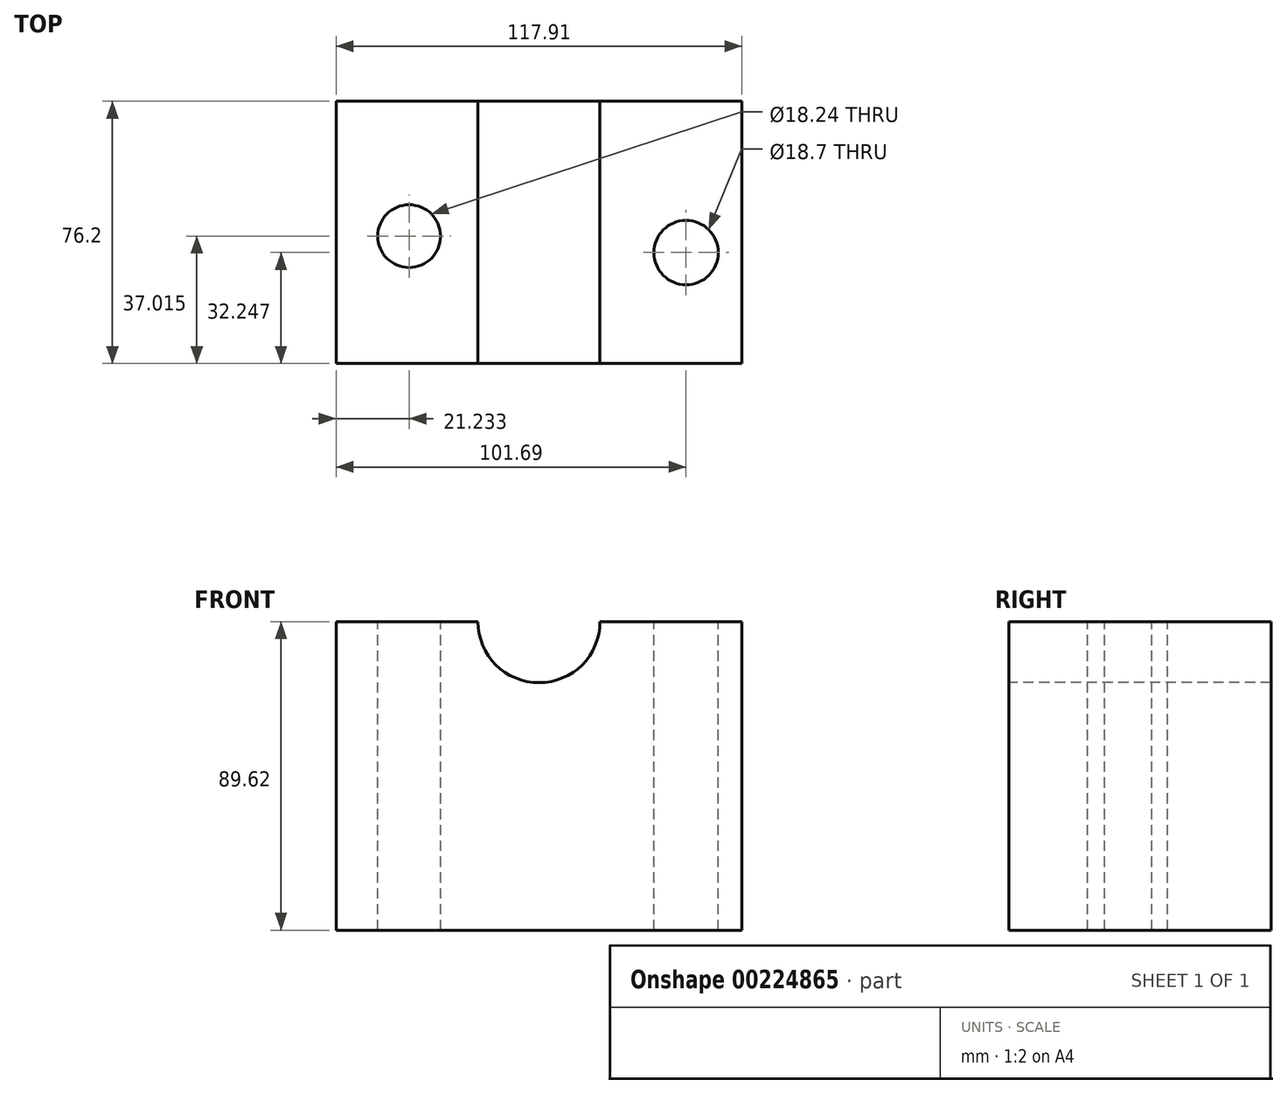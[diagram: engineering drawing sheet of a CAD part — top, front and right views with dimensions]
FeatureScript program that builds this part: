
annotation { "Feature Type Name" : "Feature", "Feature Type Description" : "" }
export const myFeature = defineFeature(function(context is Context, id is Id, definition is map)
    precondition{}
    {
        {
            var Q0;
            Q0=qCreatedBy(makeId("Front.planeOp"),FACE);
            var sketch = newSketch(context, id + "F0", { "sketchPlane" : qUnion([Q0])});
            skLineSegment(sketch, "E0.bottom", {"start": v(-58.78, 45.66) * mm, "end": v(59.13, 45.66) * mm});
            skLineSegment(sketch, "E0.top", {"start": v(-58.78, -43.96) * mm, "end": v(59.13, -43.96) * mm});
            skLineSegment(sketch, "E0.left", {"start": v(-58.78, 45.66) * mm, "end": v(-58.78, -43.96) * mm});
            skLineSegment(sketch, "E0.right", {"start": v(59.13, 45.66) * mm, "end": v(59.13, -43.96) * mm});
            skSolve(sketch);
        }
        {
            var Q0;
            Q0=makeQuery(id+"F0.imprint","IMPRINT",FACE,{"disambiguationData":[TD([[makeQuery(id+"F0.imprint","IMPRINT",EDGE,{"derivedFrom":sQuery(id+"F0.wireOp",EDGE,"E0.bottom")}),-1.0]])]});
            extrude(context, id + "F1", {"entities" : qUnion([Q0]), "depth" : 76.2 * mm});
        }
        {
            var Q0;
            Q0=makeQuery(id+"F1.opExtrude","SWEPT_FACE",FACE,{"disambiguationData":[OSD([sQuery(id+"F0.wireOp",EDGE,"E0.bottom")])]});
            var sketch = newSketch(context, id + "F2", { "sketchPlane" : qUnion([Q0])});
            skCircle(sketch, "E1", {"center": v(-37.55, -39.19) * mm, "radius": 9.12 * mm});
            skSolve(sketch);
        }
        {
            var Q0;
            Q0=makeQuery(id+"F2.imprint","IMPRINT",FACE,{"disambiguationData":[TD([[makeQuery(id+"F2.imprint","IMPRINT",EDGE,{"derivedFrom":sQuery(id+"F2.wireOp",EDGE,"E1")}),-1.0]])]});
            var sketch = newSketch(context, id + "F3", { "sketchPlane" : qUnion([Q0])});
            skCircle(sketch, "E2", {"center": v(42.91, -43.95) * mm, "radius": 9.35 * mm});
            skSolve(sketch);
        }
        {
            var Q0;
            Q0=makeQuery(id+"F2.imprint","IMPRINT",FACE,{"disambiguationData":[TD([[makeQuery(id+"F2.imprint","IMPRINT",EDGE,{"derivedFrom":sQuery(id+"F2.wireOp",EDGE,"E1")}),1.0]])]});
            extrude(context, id + "F4", {"entities" : qUnion([Q0]), "operationType" : NewBodyOperationType.REMOVE, "endBound" : BoundingType.THROUGH_ALL, "oppositeDirection" : true, "depth" : 25.4 * mm});
        }
        {
            var Q0;
            Q0=makeQuery(id+"F3.imprint","IMPRINT",FACE,{"disambiguationData":[TD([[makeQuery(id+"F3.imprint","IMPRINT",EDGE,{"derivedFrom":sQuery(id+"F3.wireOp",EDGE,"E2")}),1.0]])]});
            extrude(context, id + "F5", {"entities" : qUnion([Q0]), "operationType" : NewBodyOperationType.REMOVE, "endBound" : BoundingType.THROUGH_ALL, "oppositeDirection" : true, "depth" : 25.4 * mm});
        }
        {
            var Q0;
            Q0=makeQuery(id+"F1.opExtrude","CAP_FACE",FACE,{"disambiguationData":[OSD([sQuery(id+"F0.wireOp",EDGE,"E0.bottom"),sQuery(id+"F0.wireOp",EDGE,"E0.top"),sQuery(id+"F0.wireOp",EDGE,"E0.left"),sQuery(id+"F0.wireOp",EDGE,"E0.right")])],"isStart":false});
            var sketch = newSketch(context, id + "F6", { "sketchPlane" : qUnion([Q0])});
            skCircle(sketch, "E3", {"center": v(0.18, 45.66) * mm, "radius": 17.72 * mm});
            skSolve(sketch);
        }
        {
            var Q0;
            {var subQ0=sQuery(id+"F6.wireOp",EDGE,"E3");var subQ1=makeQuery(id+"F1.opExtrude","CAP_EDGE",EDGE,{"disambiguationData":[OSD([sQuery(id+"F0.wireOp",EDGE,"E0.bottom")])],"isStart":false});var subQ2=makeQuery(id+"F6.imprint","INTERSECT",VERTEX,{"disambiguationData":[OD(0.0)],"derivedFrom":[subQ1,subQ0]});Q0=makeQuery(id+"F6.imprint","IMPRINT",FACE,{"disambiguationData":[TD([[makeQuery(id+"F6.imprint","IMPRINT",EDGE,{"disambiguationData":[TD([[subQ2,-1.0]])],"derivedFrom":subQ0}),1.0]])]});}
            extrude(context, id + "F7", {"entities" : qUnion([Q0]), "operationType" : NewBodyOperationType.REMOVE, "endBound" : BoundingType.THROUGH_ALL, "oppositeDirection" : true, "depth" : 25.4 * mm});
        }
    });
